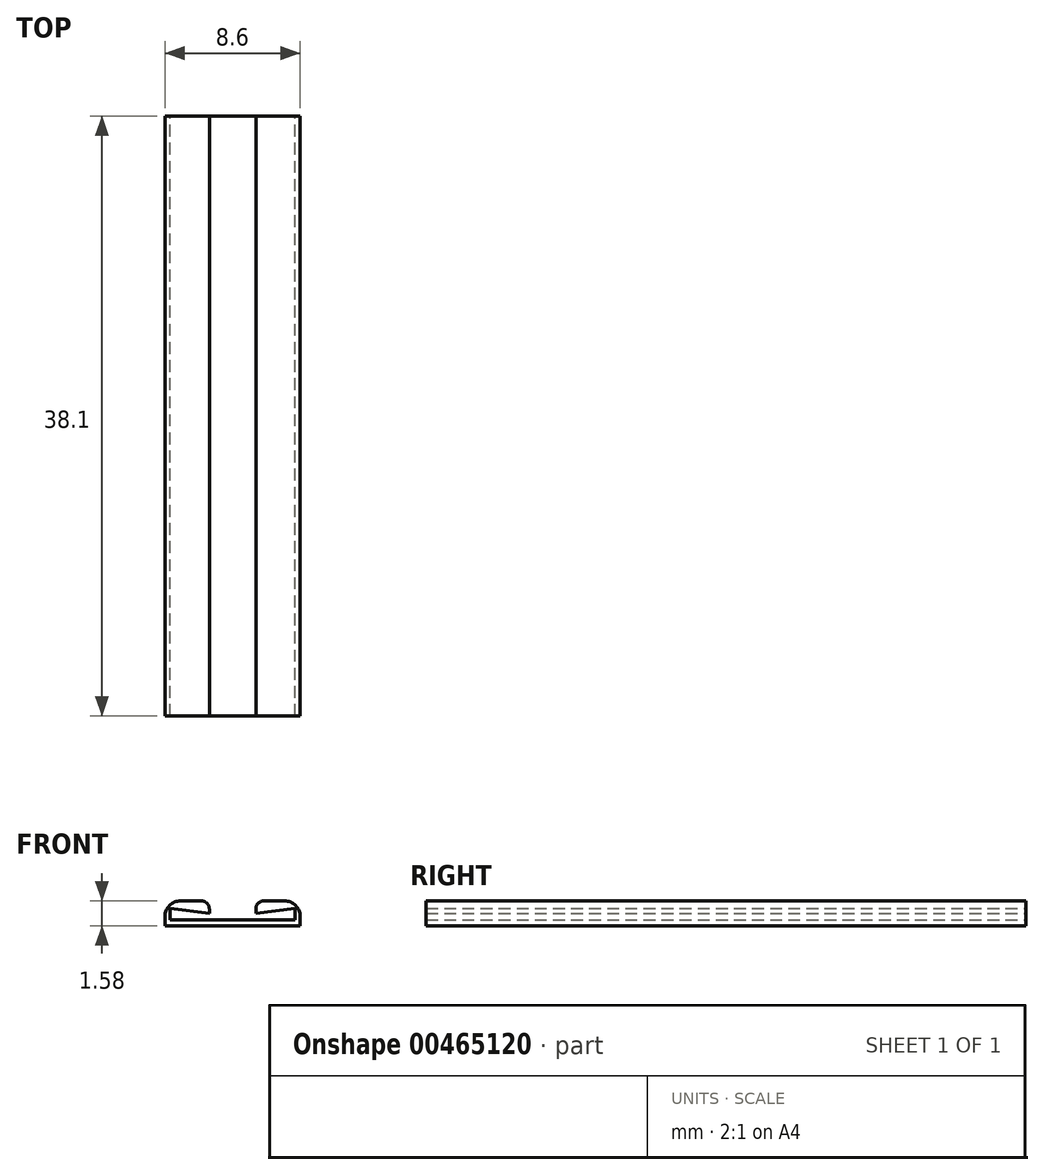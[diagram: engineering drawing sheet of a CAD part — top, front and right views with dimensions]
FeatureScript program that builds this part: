
annotation { "Feature Type Name" : "Feature", "Feature Type Description" : "" }
export const myFeature = defineFeature(function(context is Context, id is Id, definition is map)
    precondition{}
    {
        {
            var Q0;
            Q0=qCreatedBy(makeId("Front.planeOp"),FACE);
            var sketch = newSketch(context, id + "F0", { "sketchPlane" : qUnion([Q0])});
            skLineSegment(sketch, "E0.bottom", {"start": v(-4.3, -0.8) * mm, "end": v(4.3, -0.8) * mm});
            skLineSegment(sketch, "E0.left", {"start": v(-4.3, -0.8) * mm, "end": v(-4.3, 0.8) * mm});
            skLineSegment(sketch, "E0.right", {"start": v(4.3, -0.8) * mm, "end": v(4.3, 0.8) * mm});
            skPoint(sketch, "E0.middle", {"position": v(0, 0) * mm});
            skLineSegment(sketch, "E1", {"start": v(-4.3, 0.8) * mm, "end": v(-1.48, 0.8) * mm});
            skLineSegment(sketch, "E2", {"start": v(4.3, 0.8) * mm, "end": v(1.48, 0.8) * mm});
            skPoint(sketch, "E3", {"position": v(-3.96, -0.41) * mm});
            skLineSegment(sketch, "E4", {"start": v(0, 0) * mm, "end": v(0, -0.8) * mm, "construction": true});
            skPoint(sketch, "E5.MirrorP", {"position": v(3.96, -0.41) * mm});
            skLineSegment(sketch, "E6.bottom", {"start": v(-3.96, -0.41) * mm, "end": v(3.96, -0.41) * mm});
            skLineSegment(sketch, "E6.left", {"start": v(-3.96, -0.41) * mm, "end": v(-3.96, 0.32) * mm});
            skLineSegment(sketch, "E6.right", {"start": v(3.96, -0.41) * mm, "end": v(3.96, -0.41) * mm});
            skPoint(sketch, "E7", {"position": v(-1.48, 0) * mm});
            skLineSegment(sketch, "E8", {"start": v(-1.48, 0) * mm, "end": v(-3.96, 0.32) * mm});
            skLineSegment(sketch, "E9.MirrorCS", {"start": v(1.48, 0) * mm, "end": v(3.96, 0.32) * mm});
            skLineSegment(sketch, "E10", {"start": v(-1.48, 0) * mm, "end": v(-1.48, 0.8) * mm});
            skLineSegment(sketch, "E11", {"start": v(1.48, 0) * mm, "end": v(1.48, 0.8) * mm});
            skLineSegment(sketch, "E12.MirrorCS", {"start": v(3.96, -0.41) * mm, "end": v(3.96, 0.32) * mm});
            skSolve(sketch);
        }
        {
            var Q0;
            Q0=makeQuery(id+"F0.imprint","IMPRINT",FACE,{"disambiguationData":[TD([[makeQuery(id+"F0.imprint","IMPRINT",EDGE,{"derivedFrom":sQuery(id+"F0.wireOp",EDGE,"E0.bottom")}),1.0]])]});
            extrude(context, id + "F1", {"entities" : qUnion([Q0]), "depth" : 38.1 * mm});
        }
        {
            var Q0;
            Q0=makeQuery(id+"F1.opExtrude","SWEPT_EDGE",EDGE,{"disambiguationData":[OSD([sQuery(id+"F0.wireOp",EDGE,"E0.left"),sQuery(id+"F0.wireOp",EDGE,"E1")])]});
            fillet(context, id + "F2", {"entities" : qUnion([Q0]), "radius" : 1.02 * mm, "tangentPropagation" : true, "allowEdgeOverflow" : false});
        }
        {
            var Q0;
            Q0=makeQuery(id+"F1.opExtrude","SWEPT_EDGE",EDGE,{"disambiguationData":[OSD([sQuery(id+"F0.wireOp",EDGE,"E0.right"),sQuery(id+"F0.wireOp",EDGE,"E2")])]});
            fillet(context, id + "F3", {"entities" : qUnion([Q0]), "radius" : 1.02 * mm, "tangentPropagation" : true, "allowEdgeOverflow" : false});
        }
        {
            var Q0;
            Q0=makeQuery(id+"F1.opExtrude","SWEPT_EDGE",EDGE,{"disambiguationData":[OSD([sQuery(id+"F0.wireOp",EDGE,"E1"),sQuery(id+"F0.wireOp",EDGE,"E10")])]});
            fillet(context, id + "F4", {"entities" : qUnion([Q0]), "radius" : 0.5 * mm, "tangentPropagation" : true, "allowEdgeOverflow" : false});
        }
        {
            var Q0;
            Q0=makeQuery(id+"F1.opExtrude","SWEPT_EDGE",EDGE,{"disambiguationData":[OSD([sQuery(id+"F0.wireOp",EDGE,"E2"),sQuery(id+"F0.wireOp",EDGE,"E11")])]});
            fillet(context, id + "F5", {"entities" : qUnion([Q0]), "radius" : 0.5 * mm, "tangentPropagation" : true, "allowEdgeOverflow" : false});
        }
    });
